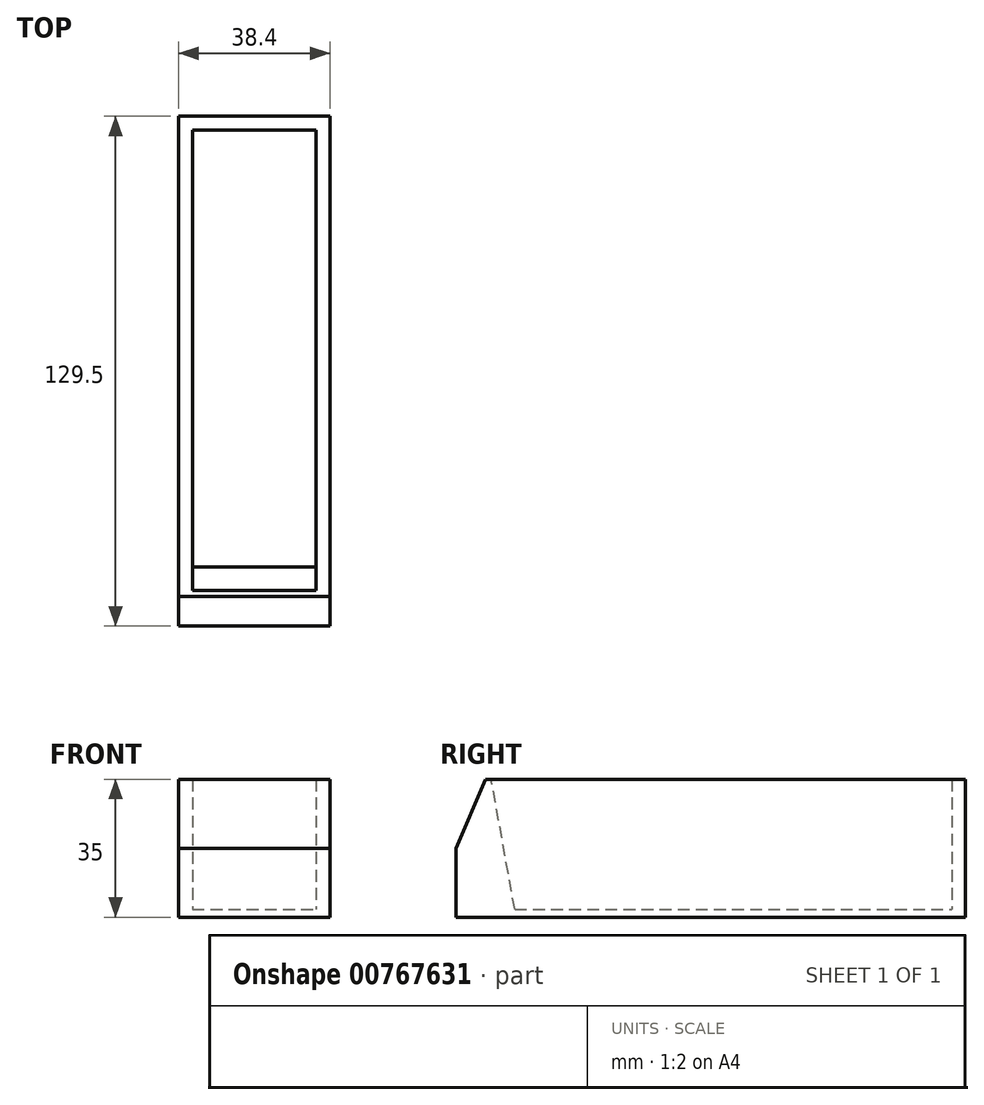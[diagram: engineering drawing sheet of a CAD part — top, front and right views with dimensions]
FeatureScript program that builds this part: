
annotation { "Feature Type Name" : "Feature", "Feature Type Description" : "" }
export const myFeature = defineFeature(function(context is Context, id is Id, definition is map)
    precondition{}
    {
        {
            var Q0;
            Q0=qCreatedBy(makeId("Top.planeOp"),FACE);
            var sketch = newSketch(context, id + "F0", { "sketchPlane" : qUnion([Q0])});
            skLineSegment(sketch, "E0.bottom", {"start": v(15.7, 55.5) * mm, "end": v(-15.7, 55.5) * mm});
            skLineSegment(sketch, "E0.top", {"start": v(15.7, -55.5) * mm, "end": v(-15.7, -55.5) * mm});
            skLineSegment(sketch, "E0.left", {"start": v(15.7, 55.5) * mm, "end": v(15.7, -55.5) * mm});
            skLineSegment(sketch, "E0.right", {"start": v(-15.7, 55.5) * mm, "end": v(-15.7, -55.5) * mm});
            skPoint(sketch, "E0.middle", {"position": v(0, 0) * mm});
            skLineSegment(sketch, "E1.bottom", {"start": v(19.2, -70.5) * mm, "end": v(-19.2, -70.5) * mm});
            skLineSegment(sketch, "E1.top", {"start": v(19.2, 59) * mm, "end": v(-19.2, 59) * mm});
            skLineSegment(sketch, "E1.left", {"start": v(19.2, -70.5) * mm, "end": v(19.2, 59) * mm});
            skLineSegment(sketch, "E1.right", {"start": v(-19.2, -70.5) * mm, "end": v(-19.2, 59) * mm});
            skPoint(sketch, "E1.middle", {"position": v(0, -5.75) * mm});
            skSolve(sketch);
        }
        {
            var Q0;
            Q0 = qSketchRegion(id + "F0", true);
            var Q1;
            Q1=makeQuery(id+"F0.imprint","IMPRINT",FACE,{"disambiguationData":[TD([[makeQuery(id+"F0.imprint","IMPRINT",EDGE,{"derivedFrom":sQuery(id+"F0.wireOp",EDGE,"E0.bottom")}),1.0]])]});
            extrude(context, id + "F1", {"entities" : qUnion([Q0, Q1]), "depth" : 2 * mm, "offsetDistance" : 25 * mm});
        }
        {
            var Q0;
            Q0=makeQuery(id+"F0.imprint","IMPRINT",FACE,{"disambiguationData":[TD([[makeQuery(id+"F0.imprint","IMPRINT",EDGE,{"derivedFrom":sQuery(id+"F0.wireOp",EDGE,"E0.bottom")}),-1.0]])]});
            extrude(context, id + "F2", {"entities" : qUnion([Q0]), "operationType" : NewBodyOperationType.ADD, "depth" : 35 * mm, "offsetDistance" : 25 * mm});
        }
        {
            var Q0;
            Q0=makeQuery(id+"F2.opExtrude","CAP_EDGE",EDGE,{"disambiguationData":[OSD([sQuery(id+"F0.wireOp",EDGE,"E1.bottom")])],"isStart":false});
            chamfer(context, id + "F3", {"entities" : qUnion([Q0]), "chamferType" : ChamferType.TWO_OFFSETS, "width1" : 7.5 * mm, "oppositeDirection" : true, "width2" : 17.5 * mm, "tangentPropagation" : true});
        }
        {
            var Q0;
            Q0=makeQuery(id+"F2.opExtrude","CAP_EDGE",EDGE,{"disambiguationData":[OSD([sQuery(id+"F0.wireOp",EDGE,"E0.top")])],"isStart":false});
            chamfer(context, id + "F4", {"entities" : qUnion([Q0]), "chamferType" : ChamferType.TWO_OFFSETS, "width1" : 6 * mm, "oppositeDirection" : false, "width2" : 33 * mm, "tangentPropagation" : true});
        }
    });
